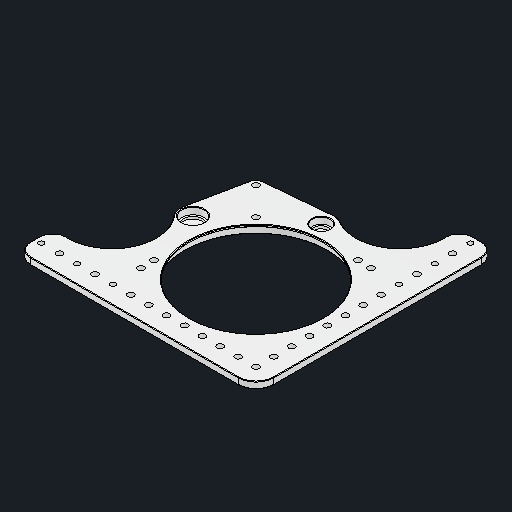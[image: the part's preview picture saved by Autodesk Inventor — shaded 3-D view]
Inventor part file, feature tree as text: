
AUTODESK INVENTOR PART (.ipt)
format: ipt  version: 2023 (Build 270158000, 158)  size: 361,984 bytes
history: native  units: in
note: dims shown in document units (in); Inventor stores cm internally (conversion verified against a paired STEP export)
features: chamfer x1
ambient origin geometry x8: Origin, YZ Plane, XZ Plane, XY Plane, X Axis, Y Axis, Z Axis, Center Point
bodies: Solid15 (feature_tree)
feature tree (1):
  chamfer  "Chamfer2"  [1 undecoded]
note: 1 required parameter value undecoded (feature->parameter linkage not recoverable at this tier; creation-order binding heuristic only, values carry confidence <= 0.55)
